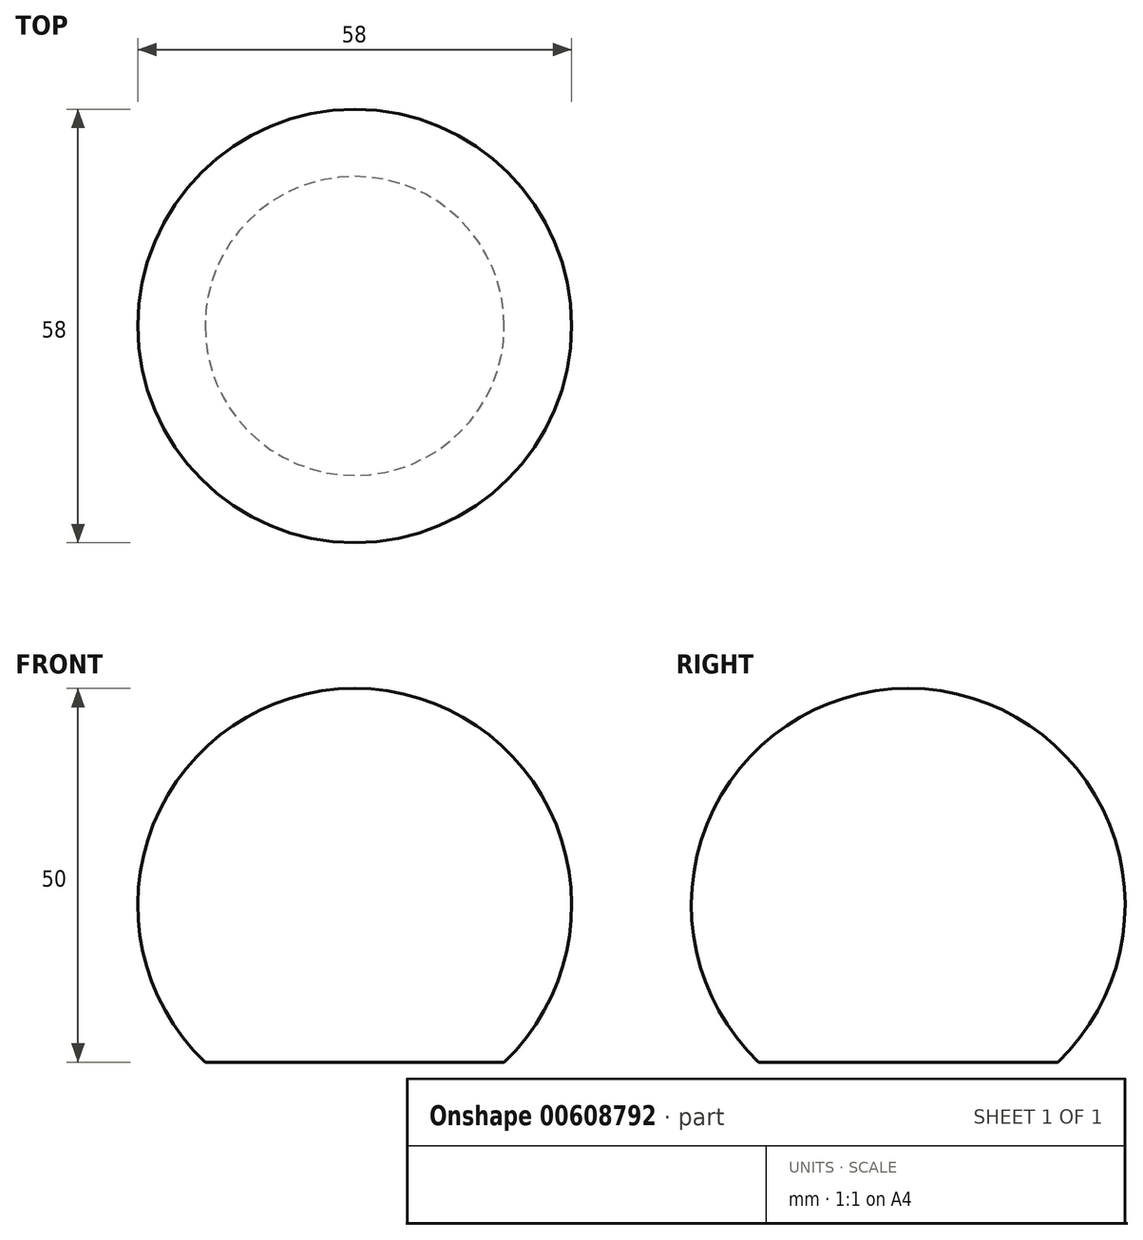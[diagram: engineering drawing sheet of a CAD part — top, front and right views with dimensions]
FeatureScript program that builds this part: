
annotation { "Feature Type Name" : "Feature", "Feature Type Description" : "" }
export const myFeature = defineFeature(function(context is Context, id is Id, definition is map)
    precondition{}
    {
        {
            var Q0;
            Q0=qCreatedBy(makeId("Front.planeOp"),FACE);
            var sketch = newSketch(context, id + "F0", { "sketchPlane" : qUnion([Q0])});
            skArc(sketch, "E0", {"start": v(19.94, 0) * mm, "mid": v(-0.06, 50) * mm, "end": v(-20.06, 0) * mm});
            skLineSegment(sketch, "E1", {"start": v(-20.06, 0) * mm, "end": v(19.94, 0) * mm});
            skLineSegment(sketch, "E2", {"start": v(-0.06, 0) * mm, "end": v(-0.06, 50) * mm});
            skSolve(sketch);
        }
        {
            var Q0;
            Q0=qCreatedBy(makeId("Front.planeOp"),FACE);
            var sketch = newSketch(context, id + "F1", { "sketchPlane" : qUnion([Q0])});
            skArc(sketch, "E3", {"start": v(21.5, 0) * mm, "mid": v(0, 38) * mm, "end": v(-21.5, 0) * mm});
            skLineSegment(sketch, "E4", {"start": v(-21.5, 0) * mm, "end": v(21.5, 0) * mm});
            skLineSegment(sketch, "E5", {"start": v(0, 0) * mm, "end": v(0, 38) * mm});
            skSolve(sketch);
        }
        {
            var Q0;
            {var subQ3=sQuery(id+"F0.wireOp",EDGE,"E2");Q0=makeQuery(id+"F0.imprint","IMPRINT",FACE,{"disambiguationData":[TD([[makeQuery(id+"F0.imprint","IMPRINT",EDGE,{"derivedFrom":subQ3}),1.0]])]});}
            var Q1;
            Q1=sQuery(id+"F1.wireOp",EDGE,"E3");
            var Q2;
            Q2=sQuery(id+"F0.wireOp",EDGE,"E2");
            revolve(context, id + "F2", {"entities" : qUnion([Q0]), "surfaceEntities" : qUnion([Q1]), "axis" : qUnion([Q2]), "revolveType" : RevolveType.ONE_DIRECTION, "angle" : 360 * degree, "surfaceOperationType" : NewSurfaceOperationType.NEW});
        }
    });
